# Revit family: IAQ-V125+IAQ-PLENUM
name_source: partatom
category: Air Terminals
revit_build: Autodesk Revit 2018 (Build: 20170223_1515(x64)
units: mm (PartAtom-declared; Revit-internal decimal feet)

## family parameters
Always vertical = No
Cut with Voids When Loaded = No
OmniClass Number = 23.75.00.00
OmniClass Title = Climate Control (HVAC)
Part Type = Normal
Room Calculation Point = No
Round Connector Dimension = Use Diameter
Shared = No
Work Plane-Based = No

## types (1)
- IAQ-V125
    Description = IAQ-V125 Valve
    Manufacturer = Nuaire
    Model = IAQ-V125
    Nuaire Model No = IAQ-V125
    Pressure Drop = 0.0 Pa
    Revit Family Last Revised = 14/03/18
    Spigot Height = 60 mm  [stored 0.19685 ft]
    Spigot Width = 204 mm
    Unit Description = IAQ-V125 Valve
    Weight = 0.00 kg

note: [stored X ft] marks values corroborated as IEEE doubles in the binary element streams (Revit-internal decimal feet)

## geometry (parser evidence)
native form markers: Blend x16, Sweep x9
no freeform markers — native parametric forms only
